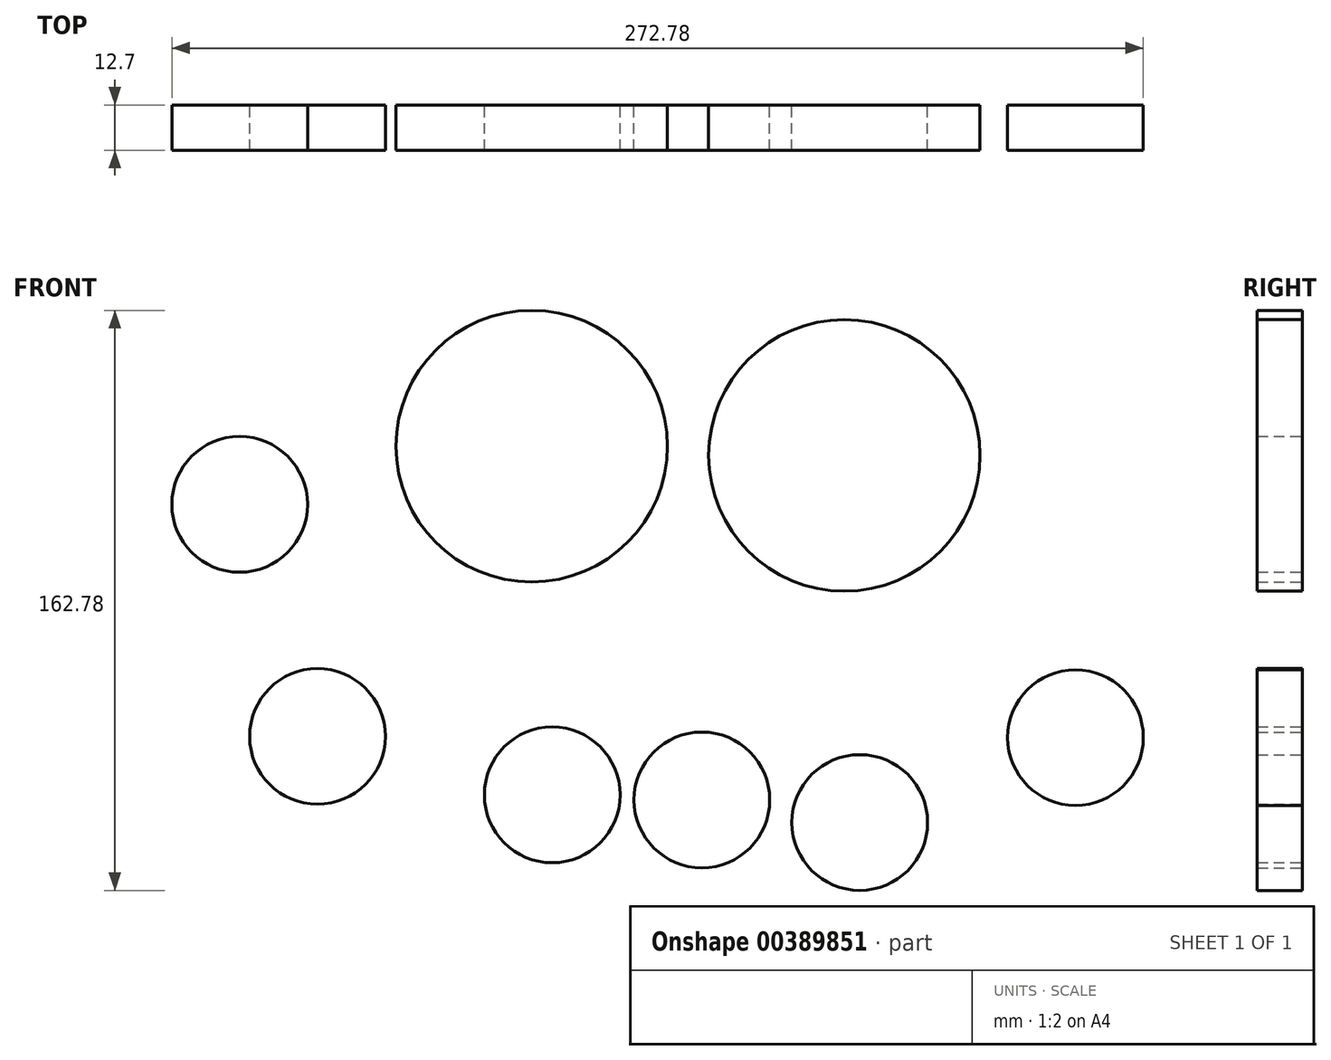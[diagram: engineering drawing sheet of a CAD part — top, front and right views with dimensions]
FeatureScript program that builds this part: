
annotation { "Feature Type Name" : "Feature", "Feature Type Description" : "" }
export const myFeature = defineFeature(function(context is Context, id is Id, definition is map)
    precondition{}
    {
        {
            var Q0;
            Q0=qCreatedBy(makeId("Front.planeOp"),FACE);
            var sketch = newSketch(context, id + "F0", { "sketchPlane" : qUnion([Q0])});
            skCircle(sketch, "E0", {"center": v(-47.78, 49.8) * mm, "radius": 38.1 * mm});
            skCircle(sketch, "E1", {"center": v(40, 47.2) * mm, "radius": 38.1 * mm});
            skCircle(sketch, "E2", {"center": v(-42.02, -48.06) * mm, "radius": 19.05 * mm});
            skCircle(sketch, "E3", {"center": v(0, -49.5) * mm, "radius": 19.05 * mm});
            skCircle(sketch, "E4", {"center": v(44.32, -55.84) * mm, "radius": 19.05 * mm});
            skCircle(sketch, "E5", {"center": v(-107.93, -31.66) * mm, "radius": 19.05 * mm});
            skCircle(sketch, "E6", {"center": v(104.9, -32) * mm, "radius": 19.05 * mm});
            skCircle(sketch, "E7", {"center": v(-129.78, 33.47) * mm, "radius": 19.05 * mm});
            skSolve(sketch);
        }
        {
            var Q0;
            Q0 = qSketchRegion(id + "F0", true);
            extrude(context, id + "F1", {"entities" : qUnion([Q0]), "depth" : 12.7 * mm});
        }
    });
